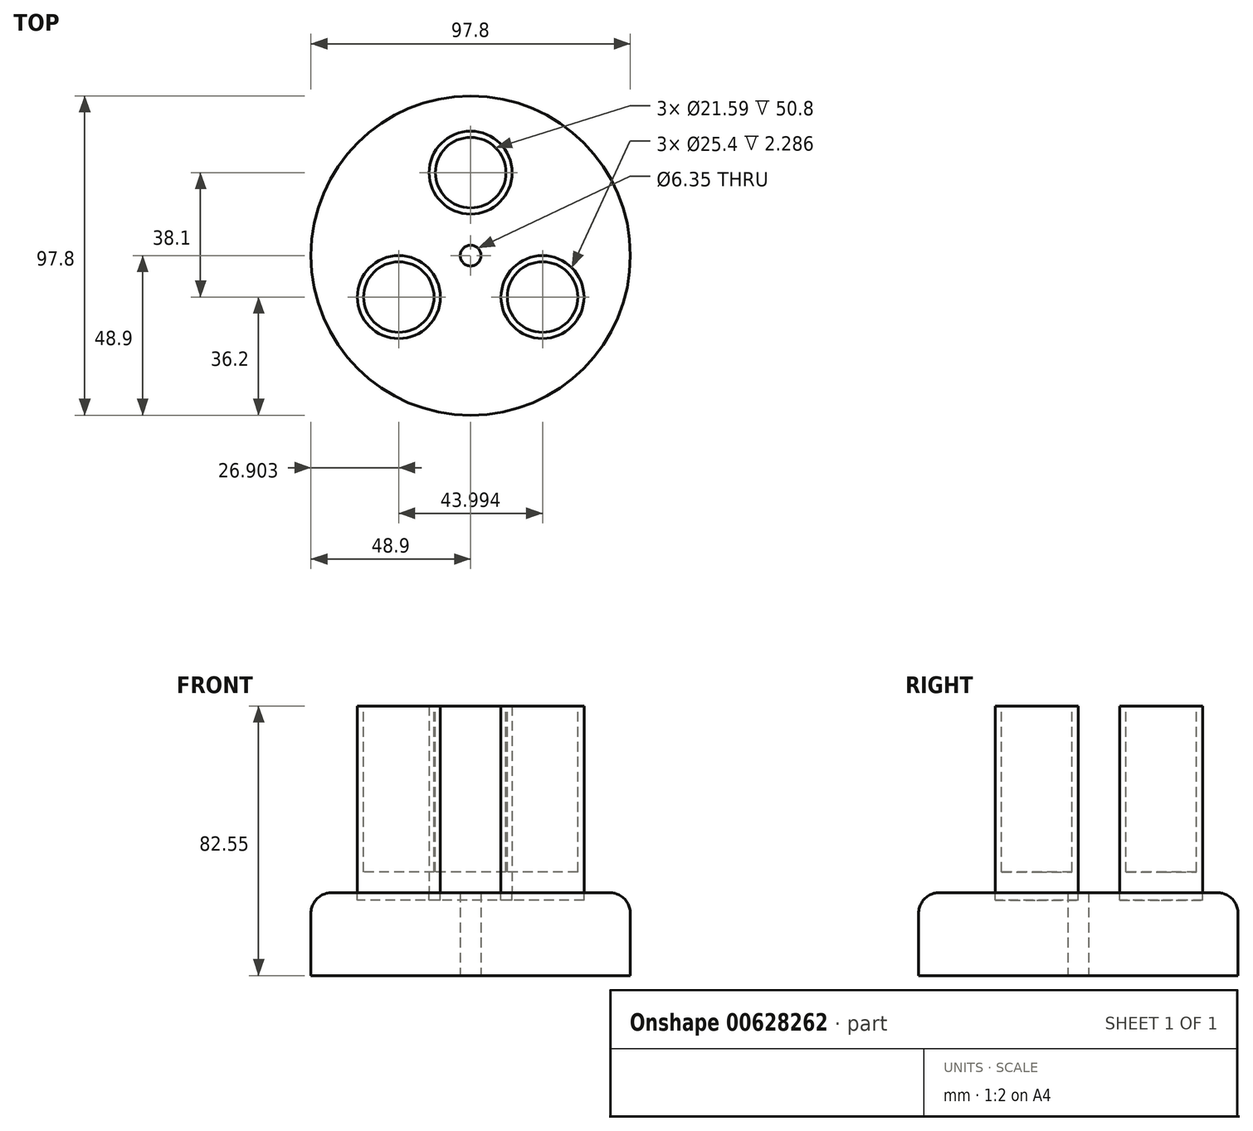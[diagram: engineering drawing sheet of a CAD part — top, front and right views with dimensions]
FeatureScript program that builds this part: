
annotation { "Feature Type Name" : "Feature", "Feature Type Description" : "" }
export const myFeature = defineFeature(function(context is Context, id is Id, definition is map)
    precondition{}
    {
        {
            var Q0;
            Q0=qCreatedBy(makeId("Top.planeOp"),FACE);
            var sketch = newSketch(context, id + "F0", { "sketchPlane" : qUnion([Q0])});
            skCircle(sketch, "E0", {"center": v(0, 0) * mm, "radius": 48.9 * mm});
            skCircle(sketch, "E1", {"center": v(0, 0) * mm, "radius": 3.18 * mm});
            skSolve(sketch);
        }
        {
            var Q0;
            Q0=makeQuery(id+"F0.imprint","IMPRINT",FACE,{"disambiguationData":[TD([[makeQuery(id+"F0.imprint","IMPRINT",EDGE,{"derivedFrom":sQuery(id+"F0.wireOp",EDGE,"E0")}),1.0]])]});
            extrude(context, id + "F1", {"entities" : qUnion([Q0]), "depth" : 25.4 * mm, "offsetDistance" : 25.4 * mm});
        }
        {
            var Q0;
            Q0=makeQuery(id+"F1.opExtrude","CAP_EDGE",EDGE,{"disambiguationData":[OSD([sQuery(id+"F0.wireOp",EDGE,"E0")])],"isStart":false});
            fillet(context, id + "F2", {"entities" : qUnion([Q0]), "radius" : 6.35 * mm, "tangentPropagation" : true, "allowEdgeOverflow" : false});
        }
        {
            var Q0;
            Q0=makeQuery(id+"F1.opExtrude","CAP_FACE",FACE,{"disambiguationData":[OSD([sQuery(id+"F0.wireOp",EDGE,"E0"),sQuery(id+"F0.wireOp",EDGE,"E1")])],"isStart":false});
            var sketch = newSketch(context, id + "F3", { "sketchPlane" : qUnion([Q0])});
            skCircle(sketch, "E2", {"center": v(0, 25.4) * mm, "radius": 12.7 * mm});
            skLineSegment(sketch, "E3", {"start": v(-148, 0) * mm, "end": v(173.13, 0) * mm, "construction": true});
            skCircle(sketch, "E4.1.0", {"center": v(-22, -12.7) * mm, "radius": 12.7 * mm});
            skCircle(sketch, "E4.2.0", {"center": v(22, -12.7) * mm, "radius": 12.7 * mm});
            skPoint(sketch, "E4.center", {"position": v(0, 0) * mm});
            skSolve(sketch);
        }
        {
            var Q0;
            Q0=makeQuery(id+"F3.imprint","IMPRINT",FACE,{"disambiguationData":[TD([[makeQuery(id+"F3.imprint","IMPRINT",EDGE,{"derivedFrom":sQuery(id+"F3.wireOp",EDGE,"E2")}),1.0]])]});
            var Q1;
            Q1=makeQuery(id+"F3.imprint","IMPRINT",FACE,{"disambiguationData":[TD([[makeQuery(id+"F3.imprint","IMPRINT",EDGE,{"derivedFrom":sQuery(id+"F3.wireOp",EDGE,"E4.1.0")}),1.0]])]});
            var Q2;
            Q2=makeQuery(id+"F3.imprint","IMPRINT",FACE,{"disambiguationData":[TD([[makeQuery(id+"F3.imprint","IMPRINT",EDGE,{"derivedFrom":sQuery(id+"F3.wireOp",EDGE,"E4.2.0")}),1.0]])]});
            extrude(context, id + "F4", {"entities" : qUnion([Q0, Q1, Q2]), "operationType" : NewBodyOperationType.ADD, "depth" : 57.15 * mm, "offsetDistance" : 25.4 * mm});
        }
        {
            var Q0;
            Q0=makeQuery(id+"F4.opExtrude","CAP_FACE",FACE,{"disambiguationData":[OSD([sQuery(id+"F3.wireOp",EDGE,"E4.2.0")])],"isStart":false});
            var sketch = newSketch(context, id + "F5", { "sketchPlane" : qUnion([Q0])});
            skCircle(sketch, "E5", {"center": v(22, -12.7) * mm, "radius": 10.8 * mm});
            skSolve(sketch);
        }
        {
            var Q0;
            Q0=makeQuery(id+"F5.imprint","IMPRINT",FACE,{"disambiguationData":[TD([[makeQuery(id+"F5.imprint","IMPRINT",EDGE,{"derivedFrom":sQuery(id+"F5.wireOp",EDGE,"E5")}),1.0]])]});
            extrude(context, id + "F6", {"entities" : qUnion([Q0]), "operationType" : NewBodyOperationType.REMOVE, "oppositeDirection" : true, "depth" : 50.8 * mm, "offsetDistance" : 25.4 * mm});
        }
        {
            var Q0;
            Q0=makeQuery(id+"F4.opExtrude","CAP_FACE",FACE,{"disambiguationData":[OSD([sQuery(id+"F3.wireOp",EDGE,"E4.1.0")])],"isStart":false});
            var sketch = newSketch(context, id + "F7", { "sketchPlane" : qUnion([Q0])});
            skCircle(sketch, "E6", {"center": v(-22, -12.7) * mm, "radius": 10.8 * mm});
            skSolve(sketch);
        }
        {
            var Q0;
            Q0=makeQuery(id+"F7.imprint","IMPRINT",FACE,{"disambiguationData":[TD([[makeQuery(id+"F7.imprint","IMPRINT",EDGE,{"derivedFrom":sQuery(id+"F7.wireOp",EDGE,"E6")}),1.0]])]});
            extrude(context, id + "F8", {"entities" : qUnion([Q0]), "operationType" : NewBodyOperationType.REMOVE, "oppositeDirection" : true, "depth" : 50.8 * mm, "offsetDistance" : 25.4 * mm});
        }
        {
            var Q0;
            Q0=makeQuery(id+"F4.opExtrude","CAP_FACE",FACE,{"disambiguationData":[OSD([sQuery(id+"F3.wireOp",EDGE,"E2")])],"isStart":false});
            var sketch = newSketch(context, id + "F9", { "sketchPlane" : qUnion([Q0])});
            skCircle(sketch, "E7", {"center": v(0, 25.4) * mm, "radius": 10.8 * mm});
            skSolve(sketch);
        }
        {
            var Q0;
            Q0=makeQuery(id+"F9.imprint","IMPRINT",FACE,{"disambiguationData":[TD([[makeQuery(id+"F9.imprint","IMPRINT",EDGE,{"derivedFrom":sQuery(id+"F9.wireOp",EDGE,"E7")}),1.0]])]});
            extrude(context, id + "F10", {"entities" : qUnion([Q0]), "operationType" : NewBodyOperationType.REMOVE, "oppositeDirection" : true, "depth" : 50.8 * mm, "offsetDistance" : 25.4 * mm});
        }
        {
            var Q0;
            Q0=qSketchRegion(id+"F3",true);
            extrude(context, id + "F11", {"entities" : qUnion([Q0]), "operationType" : NewBodyOperationType.REMOVE, "oppositeDirection" : true, "depth" : 2.3 * mm, "offsetDistance" : 25.4 * mm});
        }
    });
